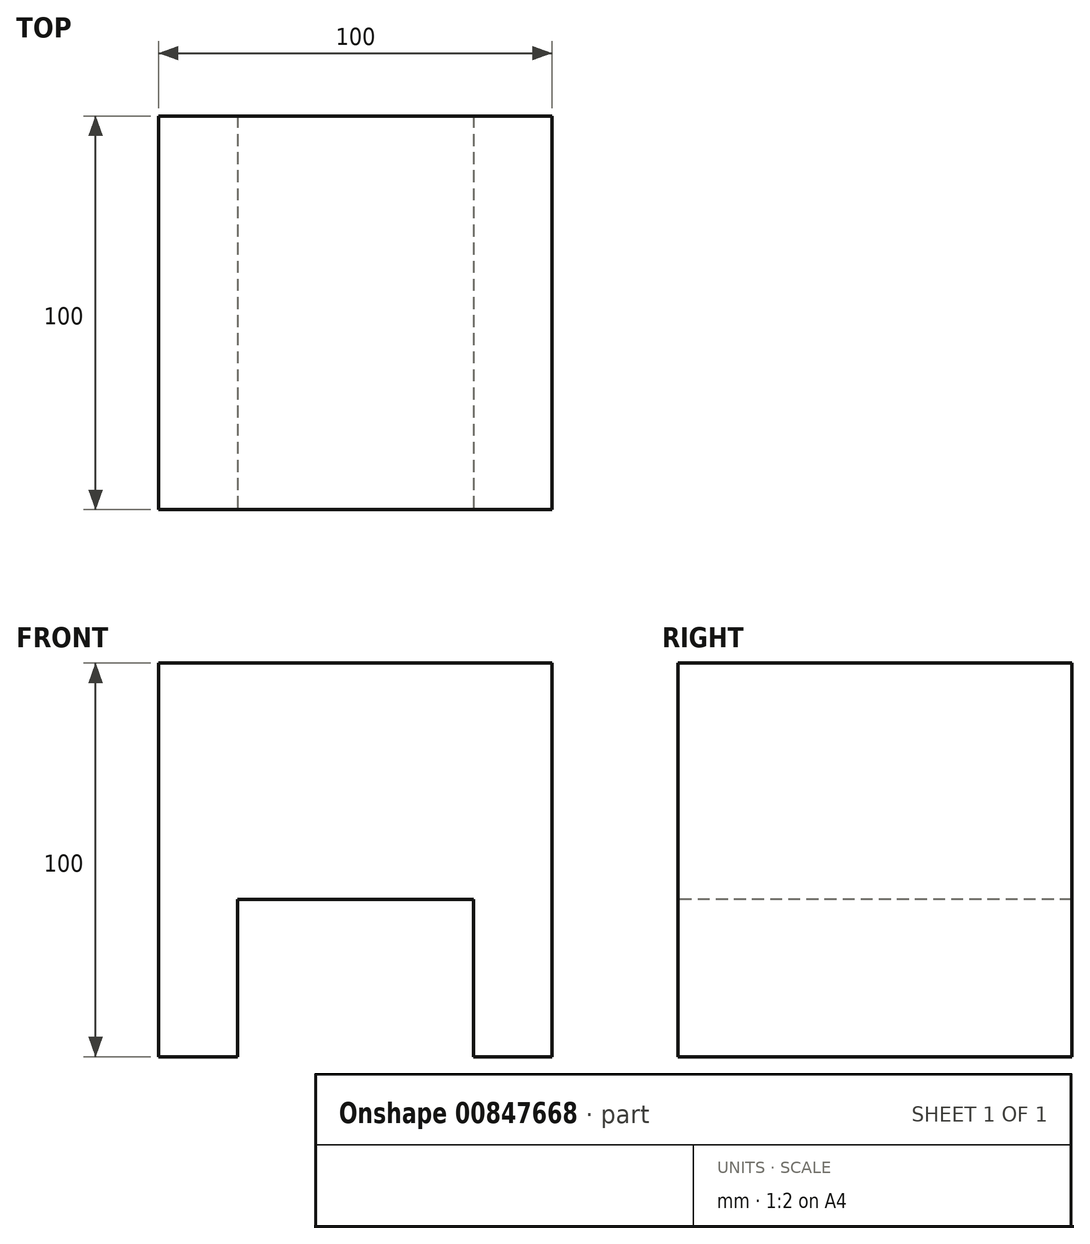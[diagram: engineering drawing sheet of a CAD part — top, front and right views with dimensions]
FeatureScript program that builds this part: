
annotation { "Feature Type Name" : "Feature", "Feature Type Description" : "" }
export const myFeature = defineFeature(function(context is Context, id is Id, definition is map)
    precondition{}
    {
        {
            var Q0;
            Q0=qCreatedBy(makeId("Top.planeOp"),FACE);
            var sketch = newSketch(context, id + "F0", { "sketchPlane" : qUnion([Q0])});
            skLineSegment(sketch, "E0.bottom", {"start": v(-50, 50) * mm, "end": v(50, 50) * mm});
            skLineSegment(sketch, "E0.top", {"start": v(-50, -50) * mm, "end": v(50, -50) * mm});
            skLineSegment(sketch, "E0.left", {"start": v(-50, 50) * mm, "end": v(-50, -50) * mm});
            skLineSegment(sketch, "E0.right", {"start": v(50, 50) * mm, "end": v(50, -50) * mm});
            skPoint(sketch, "E0.middle", {"position": v(0, 0) * mm});
            skSolve(sketch);
        }
        {
            var Q0;
            Q0 = qSketchRegion(id + "F0", true);
            extrude(context, id + "F1", {"entities" : qUnion([Q0]), "depth" : 100 * mm, "offsetDistance" : 25 * mm});
        }
        {
            var Q0;
            Q0=makeQuery(id+"F1.opExtrude","SWEPT_FACE",FACE,{"disambiguationData":[OSD([sQuery(id+"F0.wireOp",EDGE,"E0.top")])]});
            var sketch = newSketch(context, id + "F2", { "sketchPlane" : qUnion([Q0])});
            skLineSegment(sketch, "E1.bottom", {"start": v(-30, 40) * mm, "end": v(30, 40) * mm});
            skLineSegment(sketch, "E1.top", {"start": v(-30, 0) * mm, "end": v(30, 0) * mm});
            skLineSegment(sketch, "E1.left", {"start": v(-30, 40) * mm, "end": v(-30, 0) * mm});
            skLineSegment(sketch, "E1.right", {"start": v(30, 40) * mm, "end": v(30, 0) * mm});
            skSolve(sketch);
        }
        {
            var Q0;
            Q0=makeQuery(id+"F2.imprint","IMPRINT",FACE,{"disambiguationData":[TD([[makeQuery(id+"F2.imprint","IMPRINT",EDGE,{"derivedFrom":sQuery(id+"F2.wireOp",EDGE,"E1.bottom")}),-1.0]])]});
            extrude(context, id + "F3", {"entities" : qUnion([Q0]), "operationType" : NewBodyOperationType.REMOVE, "endBound" : BoundingType.THROUGH_ALL, "oppositeDirection" : true, "depth" : 25 * mm, "offsetDistance" : 25 * mm});
        }
    });
